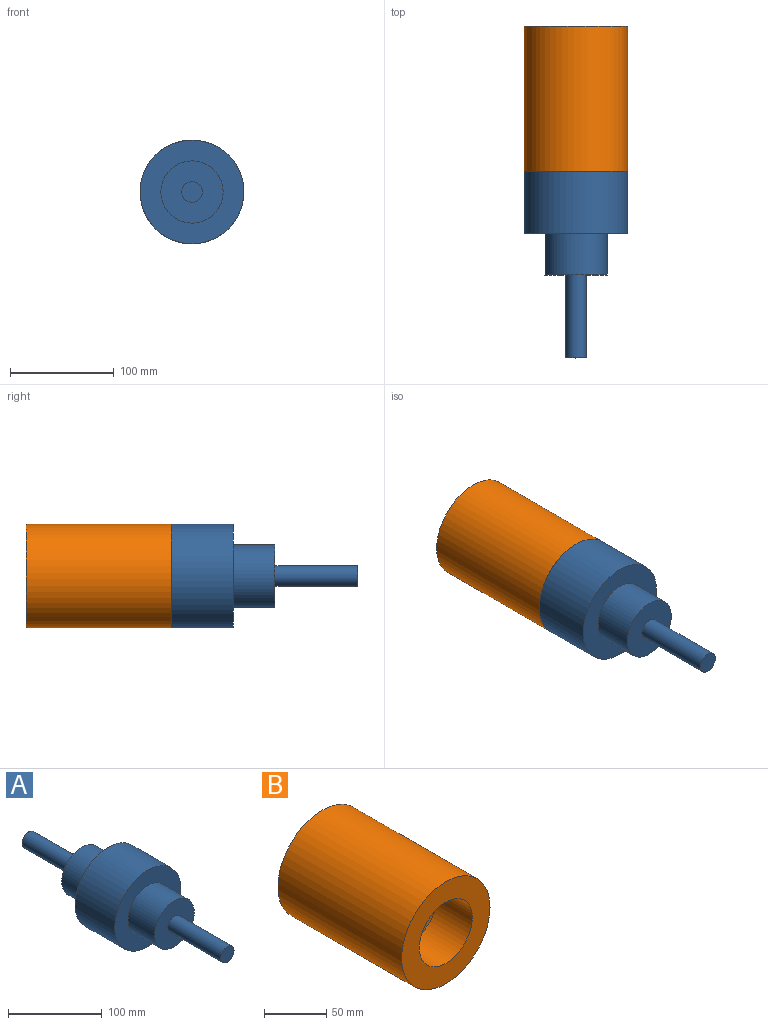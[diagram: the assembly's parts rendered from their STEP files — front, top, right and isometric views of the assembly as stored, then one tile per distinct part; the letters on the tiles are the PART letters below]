
ASSEMBLY  parts=2 mates=1
PART A: 11 faces, bbox 100x300x100 mm
  f0: cylinder r=50mm len=100mm, axis (0,1,0), area 18849.6mm2, adj f1,f2
  f1: plane 100x100mm, normal (0,-1,0), area 5026.5mm2, adj f0,f3
  f2: plane 100x100mm, normal (0,1,0), area 5026.5mm2, adj f0,f7
  f3: cylinder r=30mm len=60mm, axis (0,1,0), area 7539.8mm2, adj f1,f4
  f4: plane 60x60mm, normal (0,-1,0), area 2513.3mm2, adj f3,f5
  f5: cylinder r=10mm len=80mm, axis (0,1,0), area 5026.5mm2, adj f4,f6
  f6: plane 20x20mm, normal (0,-1,0), area 314.2mm2, adj f5
  f7: cylinder r=30mm len=60mm, axis (0,-1,0), area 7539.8mm2, adj f2,f8
  f8: plane 60x60mm, normal (0,1,0), area 2513.3mm2, adj f7,f9
  f9: cylinder r=10mm len=80mm, axis (0,-1,0), area 5026.5mm2, adj f8,f10
  f10: plane 20x20mm, normal (0,1,0), area 314.2mm2, adj f9
PART B: 7 faces, bbox 100x140x100 mm
  f0: cylinder r=50mm len=140mm, axis (0,1,0), area 43982.3mm2, adj f1,f2
  f1: plane 100x100mm, normal (0,-1,0), area 5026.5mm2, adj f0,f3
  f2: plane 100x100mm, normal (0,1,0), area 7854mm2, adj f0
  f3: cylinder r=30mm len=60mm, axis (0,-1,0), area 7539.8mm2, adj f1,f4
  f4: plane 60x60mm, normal (0,-1,0), area 2513.3mm2, adj f3,f5
  f5: cylinder r=10mm len=80mm, axis (0,-1,0), area 5026.5mm2, adj f4,f6
  f6: plane 20x20mm, normal (0,-1,0), area 314.2mm2, adj f5
PLACE A t=(-0.03,36.06,-50.88)mm
PLACE B t=(-0.03,176.06,-50.88)mm
MATE fastened B.f0 <-> A.f0  axis (0,-1,0) through (-0.03,36.06,-50.88)mm
